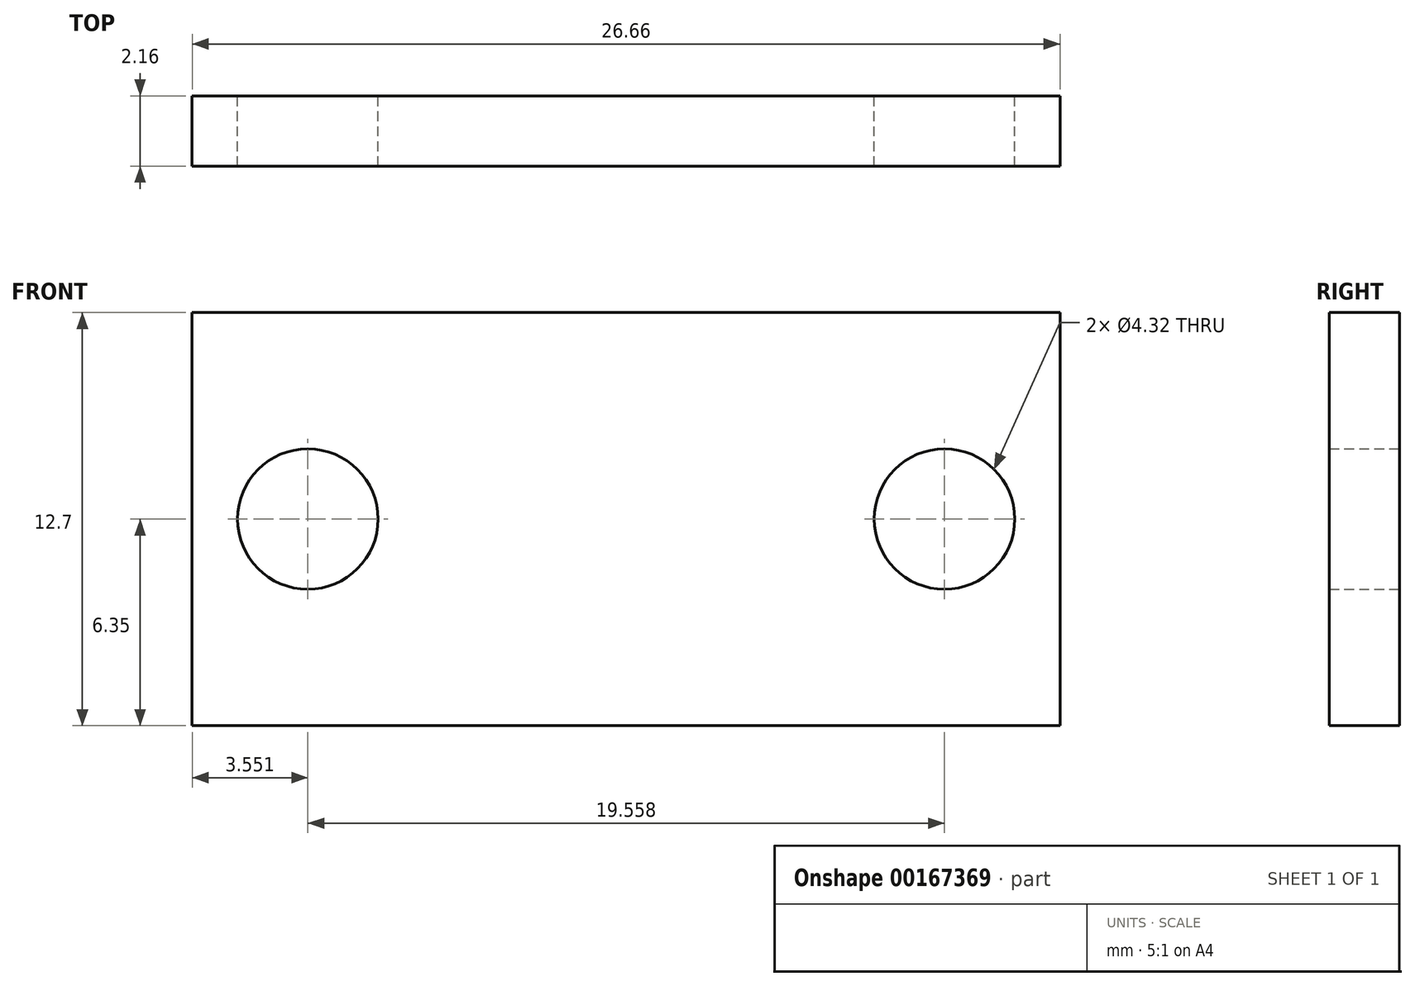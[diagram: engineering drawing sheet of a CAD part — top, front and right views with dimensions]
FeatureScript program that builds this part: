
annotation { "Feature Type Name" : "Feature", "Feature Type Description" : "" }
export const myFeature = defineFeature(function(context is Context, id is Id, definition is map)
    precondition{}
    {
        {
            var Q0;
            Q0=qCreatedBy(makeId("Front.planeOp"),FACE);
            var sketch = newSketch(context, id + "F0", { "sketchPlane" : qUnion([Q0])});
            skLineSegment(sketch, "E0.bottom", {"start": v(13.34, 6.35) * mm, "end": v(-13.34, 6.35) * mm});
            skLineSegment(sketch, "E0.top", {"start": v(13.34, -6.35) * mm, "end": v(-13.34, -6.35) * mm});
            skLineSegment(sketch, "E0.left", {"start": v(13.34, 6.35) * mm, "end": v(13.34, -6.35) * mm});
            skLineSegment(sketch, "E0.right", {"start": v(-13.34, 6.35) * mm, "end": v(-13.34, -6.35) * mm});
            skPoint(sketch, "E0.middle", {"position": v(0, 0) * mm});
            skCircle(sketch, "E1", {"center": v(-9.78, 0) * mm, "radius": 2.16 * mm});
            skCircle(sketch, "E2", {"center": v(9.78, 0) * mm, "radius": 2.16 * mm});
            skSolve(sketch);
        }
        {
            var Q0;
            Q0 = qSketchRegion(id + "F0", true);
            extrude(context, id + "F1", {"entities" : qUnion([Q0]), "depth" : 2.16 * mm});
        }
    });
